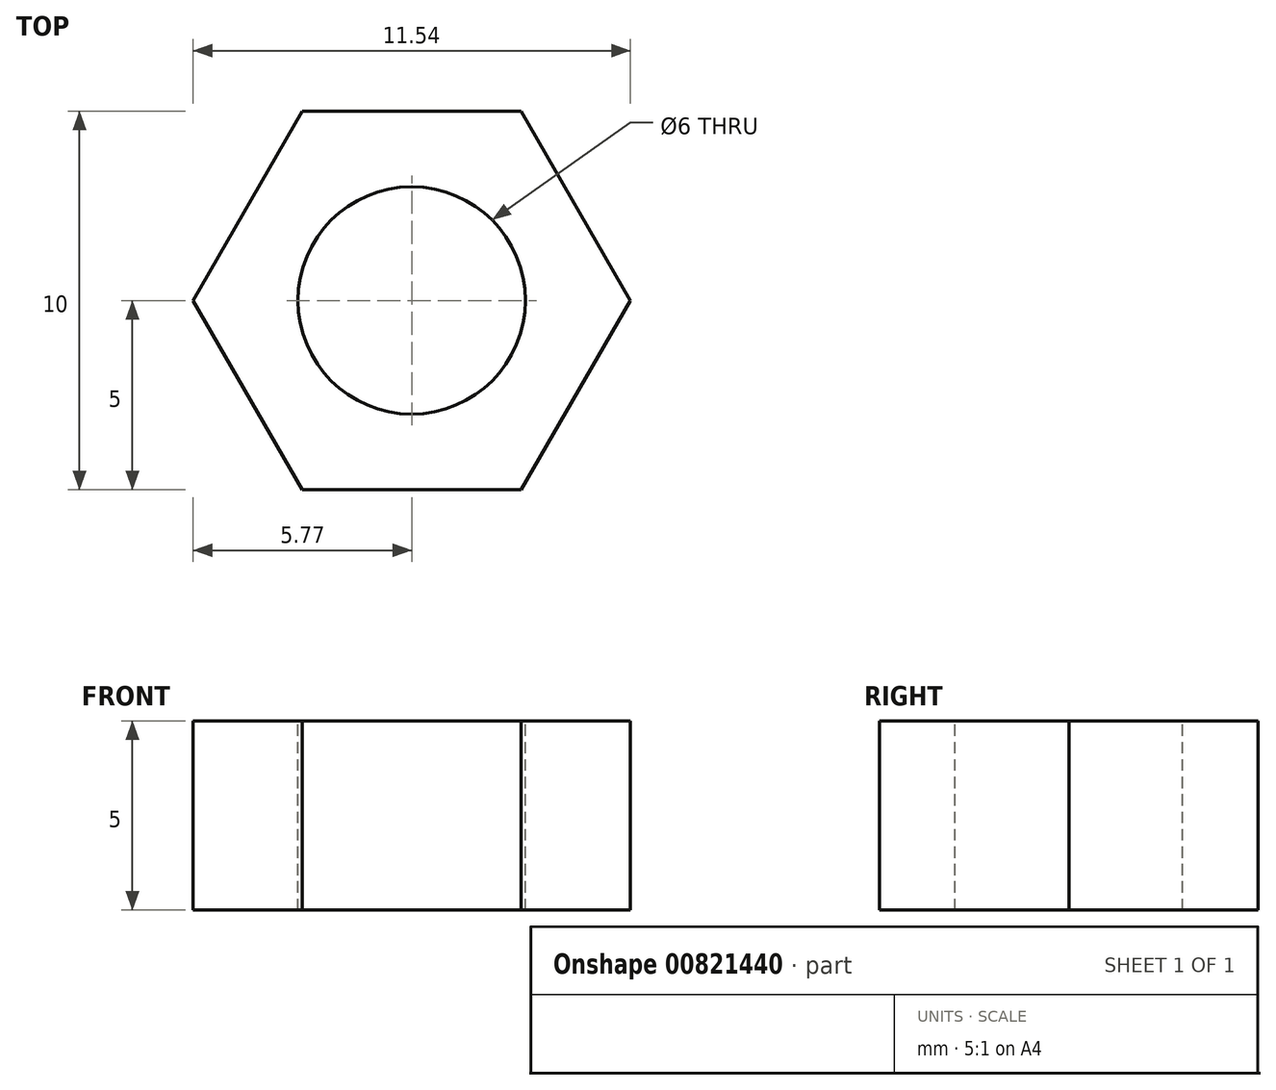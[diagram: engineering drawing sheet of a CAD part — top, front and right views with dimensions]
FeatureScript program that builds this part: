
annotation { "Feature Type Name" : "Feature", "Feature Type Description" : "" }
export const myFeature = defineFeature(function(context is Context, id is Id, definition is map)
    precondition{}
    {
        {
            var Q0;
            Q0=qCreatedBy(makeId("Top.planeOp"),FACE);
            var sketch = newSketch(context, id + "F0", { "sketchPlane" : qUnion([Q0])});
            skCircle(sketch, "E0.cCircle", {"center": v(0, 0) * mm, "radius": 5 * mm, "construction": true});
            skLineSegment(sketch, "E0.0", {"start": v(2.89, -5) * mm, "end": v(-2.89, -5) * mm});
            skLineSegment(sketch, "E0.1", {"start": v(-2.89, -5) * mm, "end": v(-5.77, 0) * mm});
            skLineSegment(sketch, "E0.2", {"start": v(-5.77, 0) * mm, "end": v(-2.89, 5) * mm});
            skLineSegment(sketch, "E0.3", {"start": v(-2.89, 5) * mm, "end": v(2.89, 5) * mm});
            skLineSegment(sketch, "E0.4", {"start": v(2.89, 5) * mm, "end": v(5.77, 0) * mm});
            skLineSegment(sketch, "E0.5", {"start": v(5.77, 0) * mm, "end": v(2.89, -5) * mm});
            skPoint(sketch, "E0.0.midPoint", {"position": v(0, -5) * mm});
            skSolve(sketch);
        }
        {
            var Q0;
            Q0 = qSketchRegion(id + "F0", true);
            extrude(context, id + "F1", {"entities" : qUnion([Q0]), "depth" : 5 * mm, "offsetDistance" : 25 * mm});
        }
        {
            var Q0;
            Q0=makeQuery(id+"F1.opExtrude","CAP_FACE",FACE,{"disambiguationData":[OSD([sQuery(id+"F0.wireOp",EDGE,"E0.0"),sQuery(id+"F0.wireOp",EDGE,"E0.1"),sQuery(id+"F0.wireOp",EDGE,"E0.2"),sQuery(id+"F0.wireOp",EDGE,"E0.3"),sQuery(id+"F0.wireOp",EDGE,"E0.4"),sQuery(id+"F0.wireOp",EDGE,"E0.5")])],"isStart":false});
            var sketch = newSketch(context, id + "F2", { "sketchPlane" : qUnion([Q0])});
            skCircle(sketch, "E1", {"center": v(0, 0) * mm, "radius": 3 * mm});
            skSolve(sketch);
        }
        {
            var Q0;
            Q0 = qSketchRegion(id + "F2", true);
            extrude(context, id + "F3", {"entities" : qUnion([Q0]), "operationType" : NewBodyOperationType.REMOVE, "endBound" : BoundingType.UP_TO_NEXT, "oppositeDirection" : true, "depth" : 25 * mm, "offsetDistance" : 25 * mm});
        }
    });
